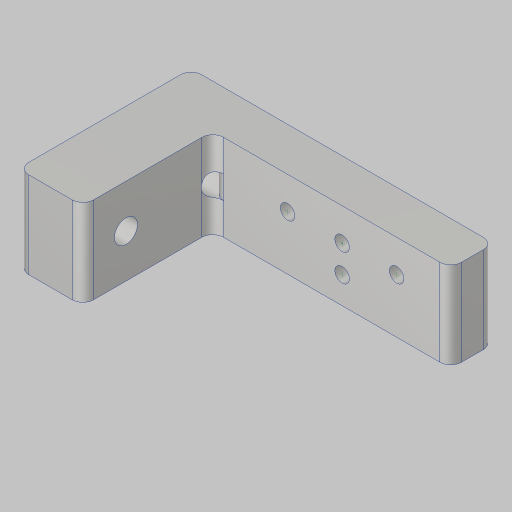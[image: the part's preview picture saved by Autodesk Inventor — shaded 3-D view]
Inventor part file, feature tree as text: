
AUTODESK INVENTOR PART (.ipt)
format: ipt  version: 2023.5 (Build 275446000, 446)  size: 223,232 bytes
history: native  units: in
note: dims shown in document units (in); Inventor stores cm internally (conversion verified against a paired STEP export)
features: sketch x4, extrude x2, hole x2, plane x2, fillet x2, projected_geometry x1
ambient origin geometry x8: Origin, YZ Plane, XZ Plane, XY Plane, X Axis, Y Axis, Z Axis, Center Point
bodies: Solid1 (feature_tree)
feature tree (13):
  sketch  "Sketch1"  dims[d0=0.6299in d1=0.6299in]
  extrude  "Extrusion1"  Depth=0.6299in
  hole  "Hole2"  [1 undecoded]
  plane  "Work Plane2"
  extrude  "Extrusion2"  Depth=3.5in
  hole  "Hole3"  [1 undecoded]
  fillet  "Fillet1"  Radius=1.005in
  fillet  "Fillet3"  Radius=2.7525in
  sketch  "Sketch2"  dims[d2=0.315in d3=0.625in]
  plane  "Work Plane1"
  sketch  "Sketch3"  dims[d4=0.375in d6=3.5in]
  projected_geometry  "Projected Loop1"
  sketch  "Sketch4"  dims[d8=1.0in d9=2.0in d10=0.0in d18=1.005in d19=0.2657in d20=0.38in d21=0.375in d22=0.25in d23=0.5635in d24=0.75in d25=0.0in d26=2.7525in d27=-2.2047in d28=0.375in d29=0.5in d30=0.75in d31=0.0in d32=0.0in d33=0.1673in d34=0.236in d35=0.375in d36=0.25in d37=0.5635in d38=0.346in d39=0.0in d40=0.125in d42=0.125in]
note: 2 required parameter values undecoded (feature->parameter linkage not recoverable at this tier; creation-order binding heuristic only, values carry confidence <= 0.55)
